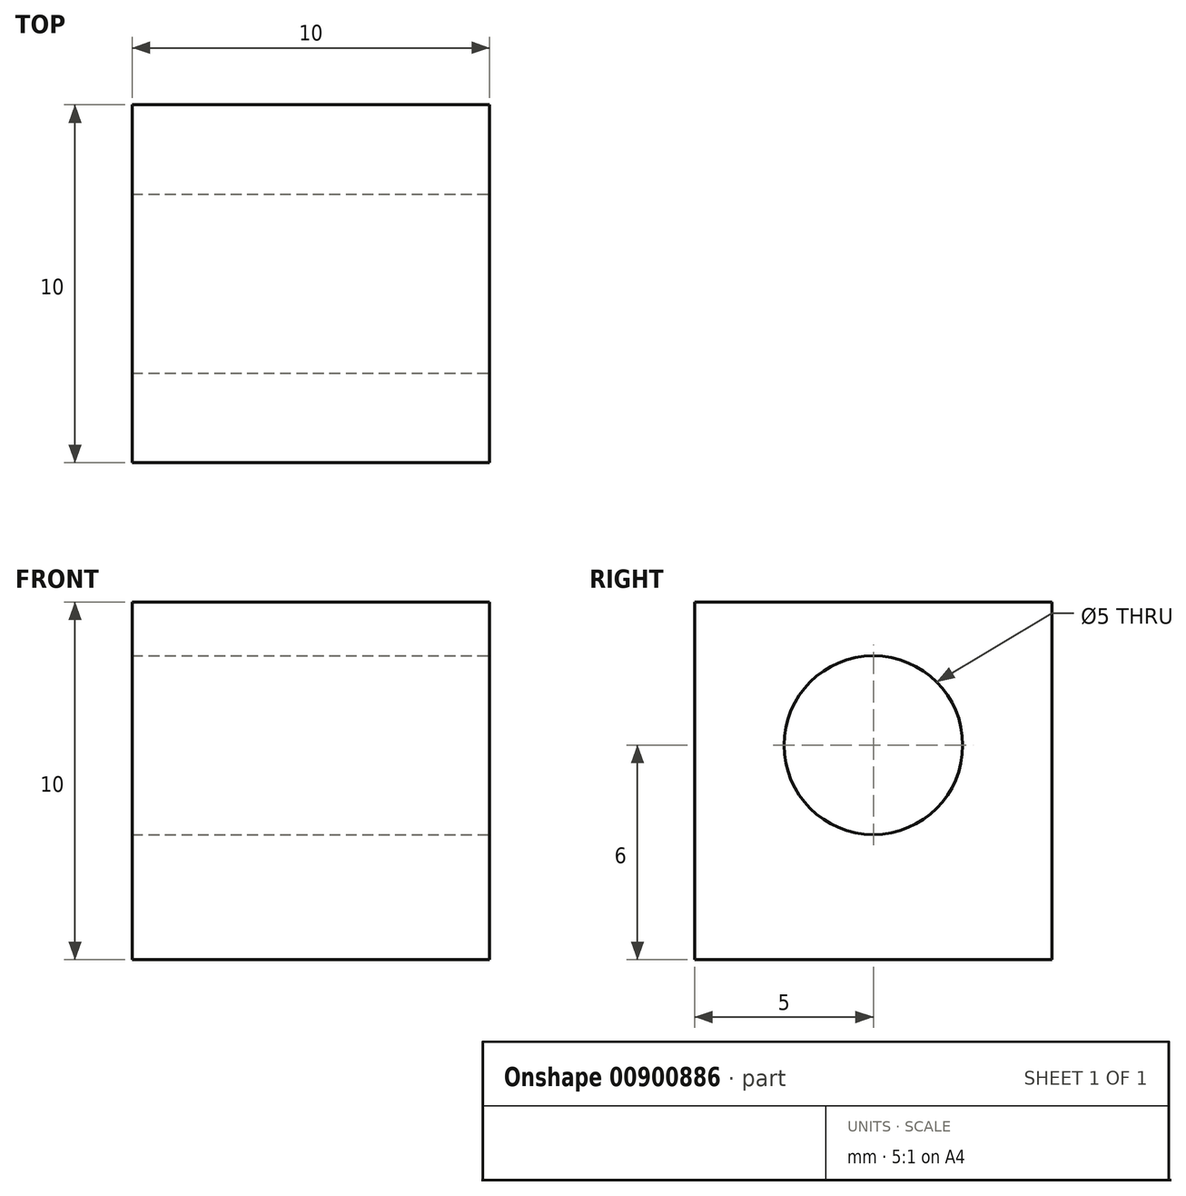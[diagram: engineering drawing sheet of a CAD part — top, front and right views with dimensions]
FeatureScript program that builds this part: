
annotation { "Feature Type Name" : "Feature", "Feature Type Description" : "" }
export const myFeature = defineFeature(function(context is Context, id is Id, definition is map)
    precondition{}
    {
        {
            var Q0;
            Q0=qCreatedBy(makeId("Top.planeOp"),FACE);
            var sketch = newSketch(context, id + "F0", { "sketchPlane" : qUnion([Q0])});
            skLineSegment(sketch, "E0.bottom", {"start": v(0, 0) * mm, "end": v(10, 0) * mm});
            skLineSegment(sketch, "E0.top", {"start": v(0, 10) * mm, "end": v(10, 10) * mm});
            skLineSegment(sketch, "E0.left", {"start": v(0, 0) * mm, "end": v(0, 10) * mm});
            skLineSegment(sketch, "E0.right", {"start": v(10, 0) * mm, "end": v(10, 10) * mm});
            skSolve(sketch);
        }
        {
            var Q0;
            Q0 = qSketchRegion(id + "F0", true);
            extrude(context, id + "F1", {"entities" : qUnion([Q0]), "depth" : 10 * mm, "offsetDistance" : 25 * mm});
        }
        {
            var Q0;
            Q0=makeQuery(id+"F1.opExtrude","SWEPT_FACE",FACE,{"disambiguationData":[OSD([sQuery(id+"F0.wireOp",EDGE,"E0.right")])]});
            var sketch = newSketch(context, id + "F2", { "sketchPlane" : qUnion([Q0])});
            skCircle(sketch, "E1", {"center": v(5, 6) * mm, "radius": 2.5 * mm});
            skSolve(sketch);
        }
        {
            var Q0;
            Q0 = qSketchRegion(id + "F2", true);
            extrude(context, id + "F3", {"entities" : qUnion([Q0]), "operationType" : NewBodyOperationType.REMOVE, "endBound" : BoundingType.UP_TO_NEXT, "oppositeDirection" : true, "depth" : 25 * mm, "offsetDistance" : 25 * mm});
        }
    });
